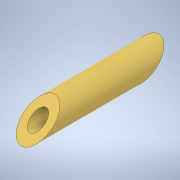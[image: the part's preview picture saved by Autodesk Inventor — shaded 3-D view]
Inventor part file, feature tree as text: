
AUTODESK INVENTOR PART (.ipt)
format: ipt  version: 2021 (Build 250183000, 183)  size: 117,248 bytes
history: native  units: mm
features: extrude x2, sketch x2
ambient origin geometry x8: Origin, YZ Plane, XZ Plane, XY Plane, X Axis, Y Axis, Z Axis, Center Point
bodies: Solid1 (feature_tree)
feature tree (4):
  extrude  "Extrusion1"  Depth=4.0mm
  extrude  "Extrusion2"  Depth=6.981317mm
  sketch  "Sketch1"  dims[d0=8.2mm d1=4.0mm]
  sketch  "Sketch2"  dims[d2=40.0mm d3=0.0mm d4=6.981317mm d5=40.0mm d6=0.0mm]
